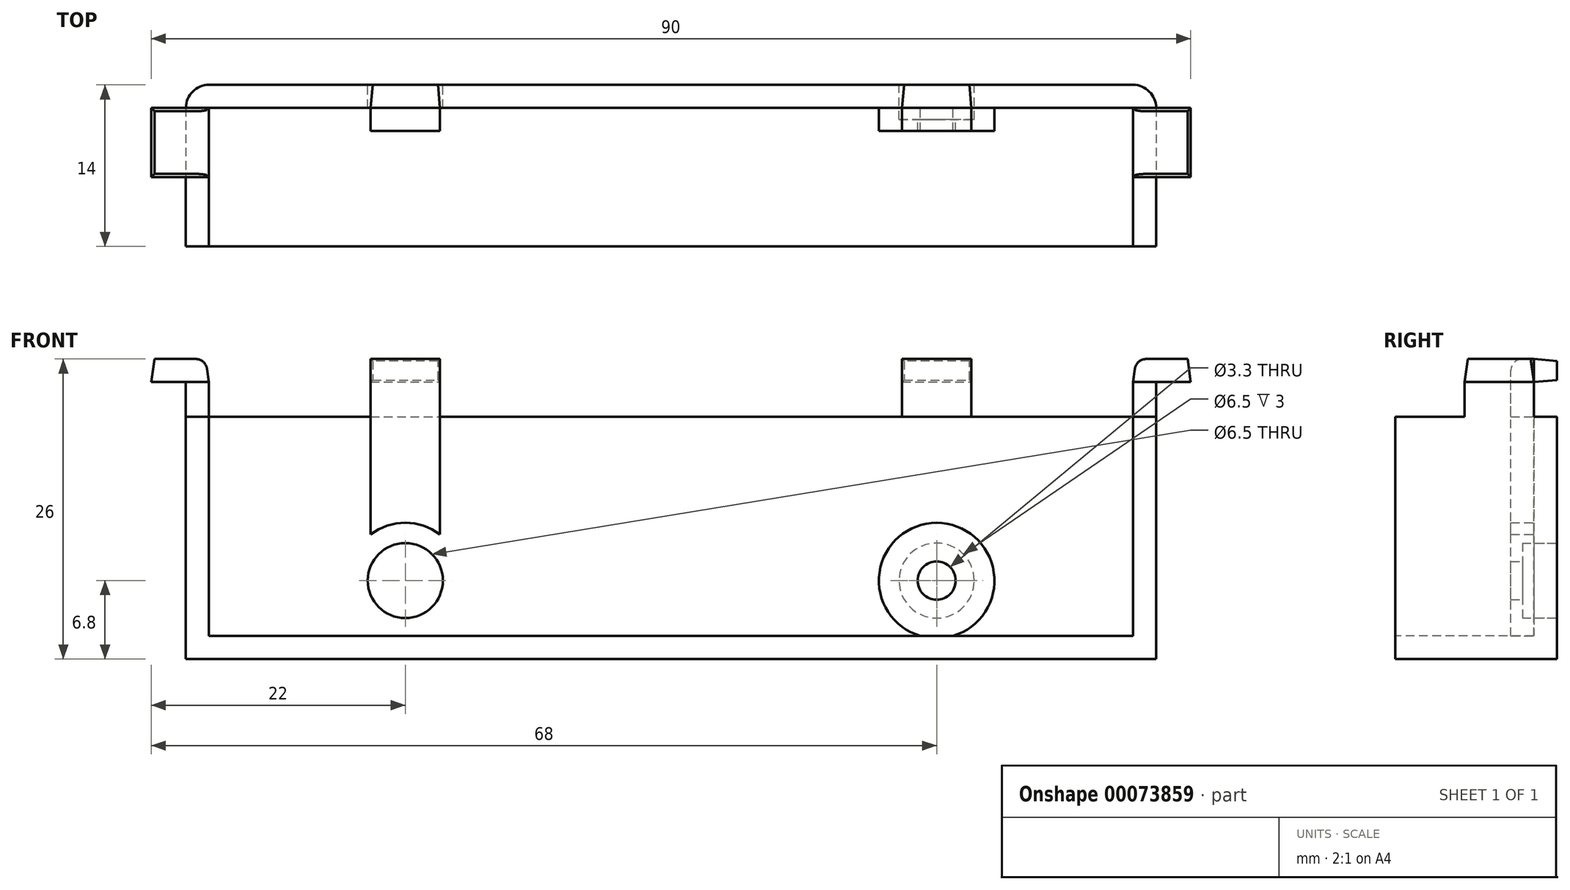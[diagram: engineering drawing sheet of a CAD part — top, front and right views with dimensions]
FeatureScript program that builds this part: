
annotation { "Feature Type Name" : "Feature", "Feature Type Description" : "" }
export const myFeature = defineFeature(function(context is Context, id is Id, definition is map)
    precondition{}
    {
        {
            var Q0;
            Q0=qCreatedBy(makeId("Top.planeOp"),FACE);
            var sketch = newSketch(context, id + "F0", { "sketchPlane" : qUnion([Q0])});
            skLineSegment(sketch, "E0.bottom", {"start": v(-40, 7) * mm, "end": v(40, 7) * mm});
            skLineSegment(sketch, "E0.top", {"start": v(-40, -5) * mm, "end": v(40, -5) * mm});
            skLineSegment(sketch, "E0.left", {"start": v(-40, 7) * mm, "end": v(-40, -5) * mm});
            skLineSegment(sketch, "E0.right", {"start": v(40, 7) * mm, "end": v(40, -5) * mm});
            skSolve(sketch);
        }
        {
            var Q0;
            Q0=makeQuery(id+"F0.imprint","IMPRINT",FACE,{"disambiguationData":[TD([[makeQuery(id+"F0.imprint","IMPRINT",EDGE,{"derivedFrom":sQuery(id+"F0.wireOp",EDGE,"E0.bottom")}),-1.0]])]});
            extrude(context, id + "F1", {"entities" : qUnion([Q0]), "depth" : 19 * mm});
        }
        {
            var Q0;
            Q0=makeQuery(id+"F1.opExtrude","CAP_FACE",FACE,{"disambiguationData":[OSD([sQuery(id+"F0.wireOp",EDGE,"E0.bottom"),sQuery(id+"F0.wireOp",EDGE,"E0.top"),sQuery(id+"F0.wireOp",EDGE,"E0.left"),sQuery(id+"F0.wireOp",EDGE,"E0.right")])],"isStart":false});
            var Q1;
            Q1=makeQuery(id+"F1.opExtrude","SWEPT_FACE",FACE,{"disambiguationData":[OSD([sQuery(id+"F0.wireOp",EDGE,"E0.top")])]});
            shell(context, id + "F2", {"entities" : qUnion([Q0, Q1]), "thickness" : 2 * mm, "oppositeDirection" : true});
        }
        {
            var Q0;
            Q0=makeQuery(id+"F1.opExtrude","SWEPT_EDGE",EDGE,{"disambiguationData":[OSD([sQuery(id+"F0.wireOp",EDGE,"E0.bottom"),sQuery(id+"F0.wireOp",EDGE,"E0.right")])]});
            var Q1;
            Q1=makeQuery(id+"F1.opExtrude","SWEPT_EDGE",EDGE,{"disambiguationData":[OSD([sQuery(id+"F0.wireOp",EDGE,"E0.bottom"),sQuery(id+"F0.wireOp",EDGE,"E0.left")])]});
            fillet(context, id + "F3", {"entities" : qUnion([Q0, Q1]), "radius" : 2 * mm, "tangentPropagation" : true, "allowEdgeOverflow" : false});
        }
        {
            var Q0;
            Q0=makeQuery(id+"F2.opShell","OFFSET_FACE",FACE,{"disambiguationData":[OSD([sQuery(id+"F0.wireOp",EDGE,"E0.bottom")])]});
            var sketch = newSketch(context, id + "F4", { "sketchPlane" : qUnion([Q0])});
            skLineSegment(sketch, "E1", {"start": v(-23, 4.8) * mm, "end": v(23, 4.8) * mm, "construction": true});
            skLineSegment(sketch, "E2", {"start": v(0, 20.96) * mm, "end": v(0, -3.74) * mm, "construction": true});
            skPoint(sketch, "E2.startSnap0", {"position": v(0, 4.8) * mm});
            skCircle(sketch, "E3", {"center": v(-23, 4.8) * mm, "radius": 5 * mm});
            skCircle(sketch, "E4.MirrorC", {"center": v(23, 4.8) * mm, "radius": 5 * mm});
            skLineSegment(sketch, "E5.top", {"start": v(-26, 24) * mm, "end": v(-20, 24) * mm});
            skLineSegment(sketch, "E5.left", {"start": v(-26, 8.8) * mm, "end": v(-26, 24) * mm});
            skLineSegment(sketch, "E5.right", {"start": v(-20, 8.8) * mm, "end": v(-20, 24) * mm});
            skLineSegment(sketch, "E6.MirrorCS", {"start": v(26, 8.8) * mm, "end": v(26, 24) * mm});
            skLineSegment(sketch, "E7.MirrorCS", {"start": v(26, 24) * mm, "end": v(20, 24) * mm});
            skLineSegment(sketch, "E8.MirrorCS", {"start": v(20, 8.8) * mm, "end": v(20, 24) * mm});
            skSolve(sketch);
        }
        {
            var Q0;
            {var subQ0=sQuery(id+"F4.wireOp",EDGE,"E3");var subQ1=sQuery(id+"F0.wireOp",EDGE,"E0.bottom");var subQ2=makeQuery(id+"F2.opShell","OFFSET_EDGE",EDGE,{"disambiguationData":[OSD([subQ1]),TDD([makeQuery(id+"F1.opExtrude","CAP_EDGE",EDGE,{"disambiguationData":[OSD([subQ1])],"isStart":true})])]});var subQ3=makeQuery(id+"F4.imprint","INTERSECT",VERTEX,{"disambiguationData":[OD(0.0)],"derivedFrom":[subQ2,subQ0]});Q0=makeQuery(id+"F4.imprint","IMPRINT",FACE,{"disambiguationData":[TD([[makeQuery(id+"F4.imprint","IMPRINT",EDGE,{"disambiguationData":[TD([[subQ3,1.0]])],"derivedFrom":subQ0}),1.0]])]});}
            var Q1;
            {var subQ0=sQuery(id+"F4.wireOp",EDGE,"E4.MirrorC");var subQ1=sQuery(id+"F0.wireOp",EDGE,"E0.bottom");var subQ2=makeQuery(id+"F2.opShell","OFFSET_EDGE",EDGE,{"disambiguationData":[OSD([subQ1]),TDD([makeQuery(id+"F1.opExtrude","CAP_EDGE",EDGE,{"disambiguationData":[OSD([subQ1])],"isStart":true})])]});var subQ3=makeQuery(id+"F4.imprint","INTERSECT",VERTEX,{"disambiguationData":[OD(0.0)],"derivedFrom":[subQ2,subQ0]});Q1=makeQuery(id+"F4.imprint","IMPRINT",FACE,{"disambiguationData":[TD([[makeQuery(id+"F4.imprint","IMPRINT",EDGE,{"disambiguationData":[TD([[subQ3,1.0]])],"derivedFrom":subQ0}),-1.0]])]});}
            extrude(context, id + "F5", {"entities" : qUnion([Q0, Q1]), "operationType" : NewBodyOperationType.ADD, "depth" : 6 * mm});
        }
        {
            var Q0;
            {var subQ0=sQuery(id+"F4.wireOp",EDGE,"E5.top");Q0=makeQuery(id+"F4.imprint","IMPRINT",FACE,{"disambiguationData":[TD([[makeQuery(id+"F4.imprint","IMPRINT",EDGE,{"derivedFrom":subQ0}),-1.0]])]});}
            var Q1;
            {var subQ0=sQuery(id+"F4.wireOp",EDGE,"E5.left");var subQ1=sQuery(id+"F4.wireOp",EDGE,"E3");var subQ2=makeQuery(id+"F4.imprint","INTERSECT",VERTEX,{"derivedFrom":[subQ1,subQ0]});Q1=makeQuery(id+"F4.imprint","IMPRINT",FACE,{"disambiguationData":[TD([[makeQuery(id+"F4.imprint","IMPRINT",EDGE,{"disambiguationData":[TD([[subQ2,1.0]])],"derivedFrom":subQ1}),-1.0]])]});}
            var Q2;
            {var subQ0=sQuery(id+"F4.wireOp",EDGE,"E6.MirrorCS");var subQ1=sQuery(id+"F4.wireOp",EDGE,"E4.MirrorC");var subQ2=makeQuery(id+"F4.imprint","INTERSECT",VERTEX,{"derivedFrom":[subQ1,subQ0]});Q2=makeQuery(id+"F4.imprint","IMPRINT",FACE,{"disambiguationData":[TD([[makeQuery(id+"F4.imprint","IMPRINT",EDGE,{"disambiguationData":[TD([[subQ2,1.0]])],"derivedFrom":subQ1}),1.0]])]});}
            var Q3;
            {var subQ0=sQuery(id+"F4.wireOp",EDGE,"E7.MirrorCS");Q3=makeQuery(id+"F4.imprint","IMPRINT",FACE,{"disambiguationData":[TD([[makeQuery(id+"F4.imprint","IMPRINT",EDGE,{"derivedFrom":subQ0}),1.0]])]});}
            extrude(context, id + "F6", {"entities" : qUnion([Q0, Q1, Q2, Q3]), "operationType" : NewBodyOperationType.ADD, "depth" : 2 * mm});
        }
        {
            var Q0;
            Q0=makeQuery(id+"F1.opExtrude","CAP_FACE",FACE,{"disambiguationData":[OSD([sQuery(id+"F0.wireOp",EDGE,"E0.bottom"),sQuery(id+"F0.wireOp",EDGE,"E0.top"),sQuery(id+"F0.wireOp",EDGE,"E0.left"),sQuery(id+"F0.wireOp",EDGE,"E0.right")])],"isStart":false});
            var sketch = newSketch(context, id + "F7", { "sketchPlane" : qUnion([Q0])});
            skLineSegment(sketch, "E9", {"start": v(0, -9) * mm, "end": v(0, 11) * mm, "construction": true});
            skPoint(sketch, "E9.endSnap0", {"position": v(0, 9) * mm});
            skLineSegment(sketch, "E10", {"start": v(-40, 7) * mm, "end": v(-42, 7) * mm});
            skLineSegment(sketch, "E11", {"start": v(-40, 1) * mm, "end": v(-42, 1) * mm});
            skLineSegment(sketch, "E12.MirrorCS", {"start": v(40, 7) * mm, "end": v(42, 7) * mm});
            skLineSegment(sketch, "E13.MirrorCS", {"start": v(40, 1) * mm, "end": v(42, 1) * mm});
            skSolve(sketch);
        }
        {
            var Q0;
            {var subQ0=sQuery(id+"F7.wireOp",EDGE,"E12.MirrorCS");Q0=makeQuery(id+"F7.imprint","IMPRINT",FACE,{"disambiguationData":[TD([[makeQuery(id+"F7.imprint","IMPRINT",EDGE,{"derivedFrom":subQ0}),-1.0]])]});}
            var Q1;
            {var subQ0=sQuery(id+"F7.wireOp",EDGE,"E10");Q1=makeQuery(id+"F7.imprint","IMPRINT",FACE,{"disambiguationData":[TD([[makeQuery(id+"F7.imprint","IMPRINT",EDGE,{"derivedFrom":subQ0}),1.0]])]});}
            extrude(context, id + "F8", {"entities" : qUnion([Q0, Q1]), "operationType" : NewBodyOperationType.ADD, "depth" : 3 * mm});
        }
        {
            var Q0;
            Q0=makeQuery(id+"F8.opExtrude","CAP_FACE",FACE,{"disambiguationData":[OSD([sQuery(id+"F0.wireOp",EDGE,"E0.left"),sQuery(id+"F7.wireOp",EDGE,"E10"),sQuery(id+"F7.wireOp",EDGE,"E11")])],"isStart":false});
            var sketch = newSketch(context, id + "F9", { "sketchPlane" : qUnion([Q0])});
            skLineSegment(sketch, "E14.bottom", {"start": v(-40, 7) * mm, "end": v(-45, 7) * mm});
            skLineSegment(sketch, "E14.top", {"start": v(-40, 1) * mm, "end": v(-45, 1) * mm});
            skLineSegment(sketch, "E14.left", {"start": v(-40, 7) * mm, "end": v(-40, 1) * mm});
            skLineSegment(sketch, "E14.right", {"start": v(-45, 7) * mm, "end": v(-45, 1) * mm});
            skPoint(sketch, "E15.0", {"position": v(-40, 7) * mm});
            skPoint(sketch, "E15.1", {"position": v(-40, 7) * mm});
            skLineSegment(sketch, "E16.bottom", {"start": v(-40, 7) * mm, "end": v(-40, 7) * mm});
            skLineSegment(sketch, "E16.top", {"start": v(-40, 12) * mm, "end": v(-40, 12) * mm});
            skLineSegment(sketch, "E16.left", {"start": v(-40, 7) * mm, "end": v(-40, 12) * mm});
            skLineSegment(sketch, "E16.right", {"start": v(-40, 7) * mm, "end": v(-40, 12) * mm});
            skLineSegment(sketch, "E17.MirrorCS", {"start": v(40, 7) * mm, "end": v(40, 7) * mm});
            skLineSegment(sketch, "E18.MirrorCS", {"start": v(40, 7) * mm, "end": v(40, 12) * mm});
            skLineSegment(sketch, "E19.MirrorCS", {"start": v(40, 12) * mm, "end": v(40, 12) * mm});
            skLineSegment(sketch, "E20.MirrorCS", {"start": v(40, 7) * mm, "end": v(45, 7) * mm});
            skLineSegment(sketch, "E21.MirrorCS", {"start": v(40, 7) * mm, "end": v(40, 1) * mm});
            skLineSegment(sketch, "E22.MirrorCS", {"start": v(40, 1) * mm, "end": v(45, 1) * mm});
            skLineSegment(sketch, "E23.MirrorCS", {"start": v(45, 7) * mm, "end": v(45, 1) * mm});
            skSolve(sketch);
        }
        {
            var Q0;
            {var subQ5=sQuery(id+"F9.wireOp",EDGE,"E14.right");Q0=makeQuery(id+"F9.imprint","IMPRINT",FACE,{"disambiguationData":[TD([[makeQuery(id+"F9.imprint","IMPRINT",EDGE,{"derivedFrom":subQ5}),1.0]])]});}
            var Q1;
            {var subQ0=sQuery(id+"F9.wireOp",EDGE,"E14.left");Q1=makeQuery(id+"F9.imprint","IMPRINT",FACE,{"disambiguationData":[TD([[makeQuery(id+"F9.imprint","IMPRINT",EDGE,{"derivedFrom":subQ0}),-1.0]])]});}
            var Q2;
            Q2=makeQuery(id+"F9.imprint","IMPRINT",FACE,{"disambiguationData":[TD([[makeQuery(id+"F9.imprint","IMPRINT",EDGE,{"derivedFrom":sQuery(id+"F9.wireOp",EDGE,"E16.bottom")}),-1.0]])]});
            var Q3;
            Q3=makeQuery(id+"F9.imprint","IMPRINT",FACE,{"disambiguationData":[TD([[makeQuery(id+"F9.imprint","IMPRINT",EDGE,{"derivedFrom":sQuery(id+"F9.wireOp",EDGE,"E17.MirrorCS")}),1.0]])]});
            var Q4;
            Q4=makeQuery(id+"F9.imprint","IMPRINT",FACE,{"disambiguationData":[TD([[makeQuery(id+"F9.imprint","IMPRINT",EDGE,{"derivedFrom":sQuery(id+"F9.wireOp",EDGE,"E20.MirrorCS")}),-1.0]])]});
            extrude(context, id + "F10", {"entities" : qUnion([Q0, Q1, Q2, Q3, Q4]), "operationType" : NewBodyOperationType.ADD, "depth" : 2 * mm, "hasDraft" : true, "draftAngle" : 8 * degree, "draftPullDirection" : true});
        }
        {
            var Q0;
            Q0=makeQuery(id+"F10.opExtrude","CAP_EDGE",EDGE,{"disambiguationData":[OSD([sQuery(id+"F9.wireOp",EDGE,"E14.left")])],"isStart":false});
            var Q1;
            Q1=makeQuery(id+"F10.opExtrude","CAP_EDGE",EDGE,{"disambiguationData":[OSD([sQuery(id+"F9.wireOp",EDGE,"E16.bottom")])],"isStart":false});
            var Q2;
            Q2=makeQuery(id+"F10.opExtrude","CAP_EDGE",EDGE,{"disambiguationData":[OSD([sQuery(id+"F9.wireOp",EDGE,"E17.MirrorCS")])],"isStart":false});
            var Q3;
            Q3=makeQuery(id+"F10.opExtrude","CAP_EDGE",EDGE,{"disambiguationData":[OSD([sQuery(id+"F9.wireOp",EDGE,"E21.MirrorCS")])],"isStart":false});
            fillet(context, id + "F11", {"entities" : qUnion([Q0, Q1, Q2, Q3]), "radius" : 1 * mm, "tangentPropagation" : true, "allowEdgeOverflow" : false});
        }
        {
            var Q0;
            Q0=makeQuery(id+"F1.opExtrude","SWEPT_FACE",FACE,{"disambiguationData":[OSD([sQuery(id+"F0.wireOp",EDGE,"E0.bottom")])]});
            var sketch = newSketch(context, id + "F12", { "sketchPlane" : qUnion([Q0])});
            skPoint(sketch, "E24.0", {"position": v(-23, 4.8) * mm});
            skPoint(sketch, "E24.1", {"position": v(23, 4.8) * mm});
            skSolve(sketch);
        }
        {
            var Q0;
            Q0=sQuery(id+"F12.wireOp",VERTEX,"E24.0");
            var Q1;
            Q1=sQuery(id+"F12.wireOp",VERTEX,"E24.1");
            var Q2;
            Q2=makeQuery(id+"F1.opExtrude","SWEPT_BODY",BODY,{"disambiguationData":[OSD([sQuery(id+"F0.wireOp",EDGE,"E0.bottom"),sQuery(id+"F0.wireOp",EDGE,"E0.top"),sQuery(id+"F0.wireOp",EDGE,"E0.left"),sQuery(id+"F0.wireOp",EDGE,"E0.right")])]});
            hole(context, id + "F13", {"style" : HoleStyle.C_BORE, "endStyle" : HoleEndStyle.THROUGH, "standardTappedOrClearance" : lookupTablePath({ "standard" : "ISO", "fit" : "Normal", "size" : "M3", "type" : "Clearance" }), "standardBlindInLast" : lookupTablePath({ "fit" : "Standard", "standard" : "ISO", "size" : "M3", "type" : "Clearance" }), "holeDiameter" : 3.3 * mm, "cBoreDiameter" : 6.5 * mm, "cBoreDepth" : 3 * mm, "locations" : qUnion([Q0, Q1]), "scope" : qUnion([Q2]), "isTappedThrough" : true});
        }
        {
            var Q0;
            {var subQ0=sQuery(id+"F4.wireOp",EDGE,"E7.MirrorCS");Q0=makeQuery(id+"F4.imprint","IMPRINT",FACE,{"disambiguationData":[TD([[makeQuery(id+"F4.imprint","IMPRINT",EDGE,{"derivedFrom":subQ0}),1.0]])]});}
            var sketch = newSketch(context, id + "F14", { "sketchPlane" : qUnion([Q0])});
            skPoint(sketch, "E25.0", {"position": v(-26, 24) * mm});
            skPoint(sketch, "E25.1", {"position": v(-20, 24) * mm});
            skPoint(sketch, "E25.2", {"position": v(20, 24) * mm});
            skPoint(sketch, "E25.3", {"position": v(26, 24) * mm});
            skLineSegment(sketch, "E26.bottom", {"start": v(-26, 24) * mm, "end": v(-20, 24) * mm});
            skLineSegment(sketch, "E26.top", {"start": v(-26, 22) * mm, "end": v(-20, 22) * mm});
            skLineSegment(sketch, "E26.left", {"start": v(-26, 24) * mm, "end": v(-26, 22) * mm});
            skLineSegment(sketch, "E26.right", {"start": v(-20, 24) * mm, "end": v(-20, 22) * mm});
            skLineSegment(sketch, "E27.bottom", {"start": v(20, 24) * mm, "end": v(26, 24) * mm});
            skLineSegment(sketch, "E27.top", {"start": v(20, 22) * mm, "end": v(26, 22) * mm});
            skLineSegment(sketch, "E27.left", {"start": v(20, 24) * mm, "end": v(20, 22) * mm});
            skLineSegment(sketch, "E27.right", {"start": v(26, 24) * mm, "end": v(26, 22) * mm});
            skSolve(sketch);
        }
        {
            var Q0;
            Q0=makeQuery(id+"F14.imprint","IMPRINT",FACE,{"disambiguationData":[TD([[makeQuery(id+"F14.imprint","IMPRINT",EDGE,{"derivedFrom":sQuery(id+"F14.wireOp",EDGE,"E27.bottom")}),1.0]])]});
            var Q1;
            Q1=makeQuery(id+"F14.imprint","IMPRINT",FACE,{"disambiguationData":[TD([[makeQuery(id+"F14.imprint","IMPRINT",EDGE,{"derivedFrom":sQuery(id+"F14.wireOp",EDGE,"E26.bottom")}),-1.0]])]});
            extrude(context, id + "F15", {"entities" : qUnion([Q0, Q1]), "operationType" : NewBodyOperationType.ADD, "oppositeDirection" : true, "depth" : 2 * mm, "hasDraft" : true, "draftAngle" : 5 * degree, "draftPullDirection" : true});
        }
        {
            var Q0;
            Q0=makeQuery(id+"F6.opExtrude","CAP_EDGE",EDGE,{"disambiguationData":[OSD([sQuery(id+"F4.wireOp",EDGE,"E7.MirrorCS")])],"isStart":false});
            var Q1;
            Q1=makeQuery(id+"F6.opExtrude","CAP_EDGE",EDGE,{"disambiguationData":[OSD([sQuery(id+"F4.wireOp",EDGE,"E5.top")])],"isStart":false});
            fillet(context, id + "F16", {"entities" : qUnion([Q0, Q1]), "radius" : 1 * mm, "tangentPropagation" : true, "allowEdgeOverflow" : false});
        }
    });
